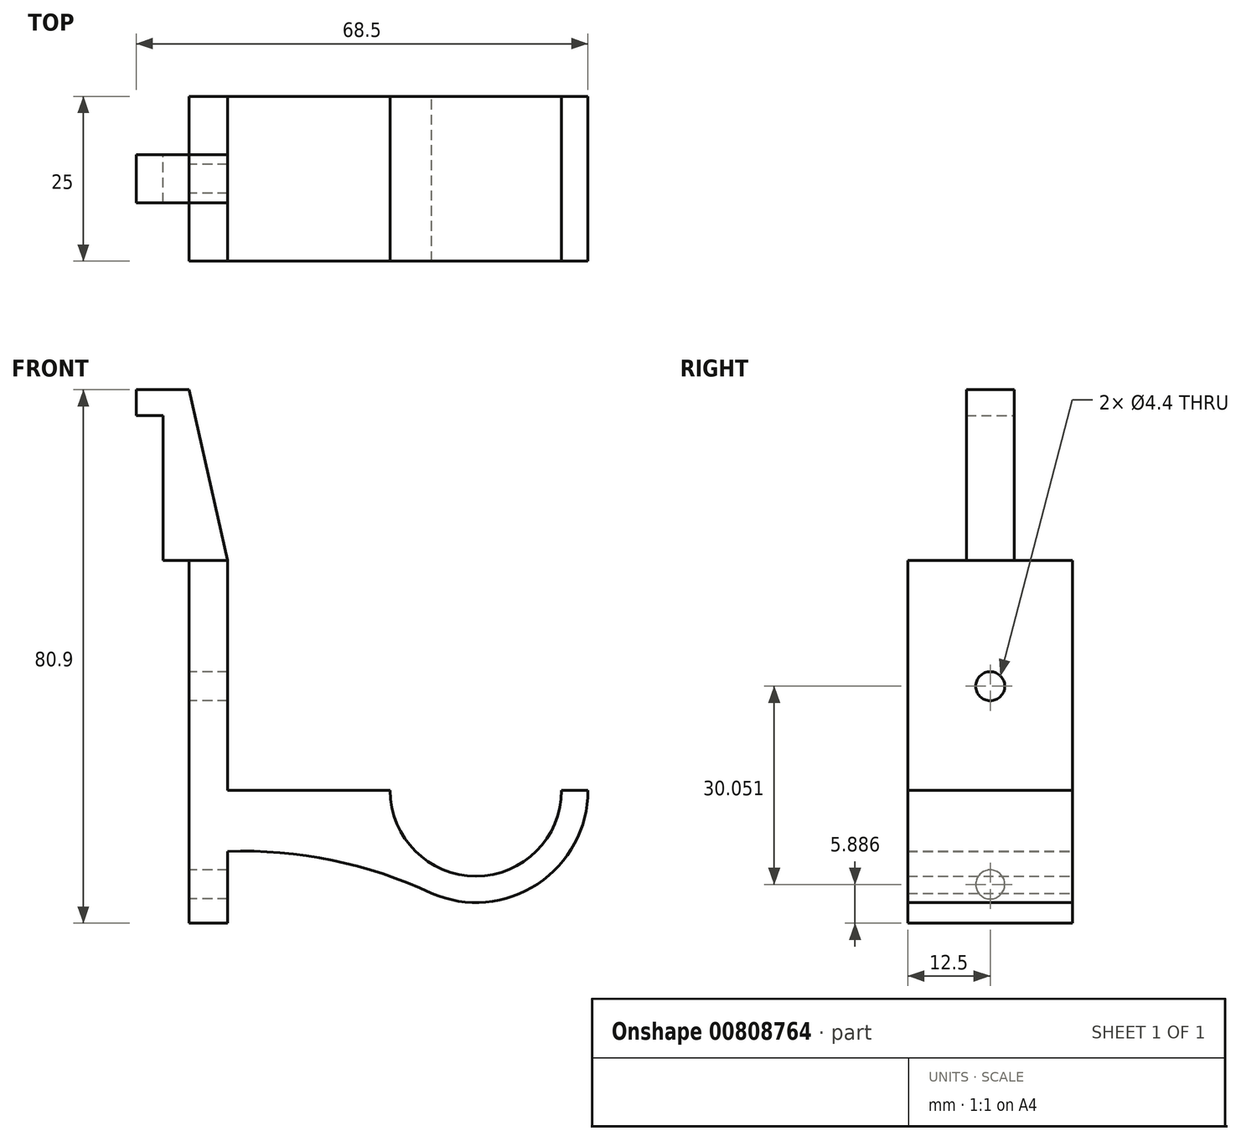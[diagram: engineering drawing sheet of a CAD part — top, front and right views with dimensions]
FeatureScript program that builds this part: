
annotation { "Feature Type Name" : "Feature", "Feature Type Description" : "" }
export const myFeature = defineFeature(function(context is Context, id is Id, definition is map)
    precondition{}
    {
        {
            var Q0;
            Q0=qCreatedBy(makeId("Front.planeOp"),FACE);
            var sketch = newSketch(context, id + "F0", { "sketchPlane" : qUnion([Q0])});
            skLineSegment(sketch, "E0.bottom", {"start": v(-6.93, 34.86) * mm, "end": v(-1.13, 34.86) * mm});
            skLineSegment(sketch, "E0.top", {"start": v(-6.93, -20.14) * mm, "end": v(-1.13, -20.14) * mm});
            skLineSegment(sketch, "E0.left", {"start": v(-6.93, 34.86) * mm, "end": v(-6.93, -20.14) * mm});
            skLineSegment(sketch, "E0.right", {"start": v(-1.13, 34.86) * mm, "end": v(-1.13, -20.14) * mm});
            skLineSegment(sketch, "E1", {"start": v(-6.93, 15.76) * mm, "end": v(-1.13, 15.76) * mm});
            skLineSegment(sketch, "E2", {"start": v(-6.93, -14.24) * mm, "end": v(-1.13, -14.24) * mm});
            skLineSegment(sketch, "E3", {"start": v(-6.93, 34.86) * mm, "end": v(-10.93, 34.86) * mm});
            skLineSegment(sketch, "E4", {"start": v(-10.93, 34.86) * mm, "end": v(-10.93, 56.86) * mm});
            skLineSegment(sketch, "E5", {"start": v(-10.93, 56.86) * mm, "end": v(-15, 56.86) * mm});
            skLineSegment(sketch, "E6", {"start": v(-15, 56.86) * mm, "end": v(-15, 60.76) * mm});
            skLineSegment(sketch, "E7", {"start": v(-15, 60.76) * mm, "end": v(-6.93, 60.76) * mm});
            skLineSegment(sketch, "E8", {"start": v(-6.93, 60.76) * mm, "end": v(-1.13, 34.86) * mm});
            skArc(sketch, "E9", {"start": v(23.53, 0) * mm, "mid": v(36.52, -13) * mm, "end": v(49.51, 0) * mm});
            skArc(sketch, "E10.0", {"start": v(19.53, 0) * mm, "mid": v(36.52, -17) * mm, "end": v(53.51, 0) * mm});
            skArc(sketch, "E11", {"start": v(29.82, -15.62) * mm, "mid": v(14.72, -10.58) * mm, "end": v(-1.13, -9.24) * mm});
            skLineSegment(sketch, "E12", {"start": v(19.53, 0) * mm, "end": v(23.53, 0) * mm});
            skLineSegment(sketch, "E13", {"start": v(53.51, 0) * mm, "end": v(53.51, 0) * mm});
            skLineSegment(sketch, "E14", {"start": v(49.51, 0) * mm, "end": v(53.51, 0) * mm});
            skLineSegment(sketch, "E15", {"start": v(19.53, 0) * mm, "end": v(-1.13, 0) * mm});
            skPoint(sketch, "E15.endSnap0", {"position": v(-1.13, 7.36) * mm});
            skSolve(sketch);
        }
        {
            var Q0;
            {var subQ0=sQuery(id+"F0.wireOp",EDGE,"E0.top");Q0=makeQuery(id+"F0.imprint","IMPRINT",FACE,{"disambiguationData":[TD([[makeQuery(id+"F0.imprint","IMPRINT",EDGE,{"derivedFrom":subQ0}),1.0]])]});}
            var Q1;
            {var subQ0=sQuery(id+"F0.wireOp",EDGE,"E11");var subQ1=sQuery(id+"F0.wireOp",EDGE,"E10.0");var subQ2=makeQuery(id+"F0.imprint","INTERSECT",VERTEX,{"disambiguationData":[OD(0.0)],"derivedFrom":[subQ1,subQ0]});Q1=makeQuery(id+"F0.imprint","IMPRINT",FACE,{"disambiguationData":[TD([[makeQuery(id+"F0.imprint","IMPRINT",EDGE,{"disambiguationData":[TD([[subQ2,1.0]])],"derivedFrom":subQ1}),1.0]])]});}
            var Q2;
            {var subQ0=sQuery(id+"F0.wireOp",EDGE,"E0.bottom");Q2=makeQuery(id+"F0.imprint","IMPRINT",FACE,{"disambiguationData":[TD([[makeQuery(id+"F0.imprint","IMPRINT",EDGE,{"derivedFrom":subQ0}),-1.0]])]});}
            var Q3;
            {var subQ3=sQuery(id+"F0.wireOp",EDGE,"E15");Q3=makeQuery(id+"F0.imprint","IMPRINT",FACE,{"disambiguationData":[TD([[makeQuery(id+"F0.imprint","IMPRINT",EDGE,{"derivedFrom":subQ3}),1.0]])]});}
            var Q4;
            Q4=makeQuery(id+"F0.imprint","IMPRINT",FACE,{"disambiguationData":[TD([[makeQuery(id+"F0.imprint","IMPRINT",EDGE,{"derivedFrom":sQuery(id+"F0.wireOp",EDGE,"E9")}),-1.0]])]});
            var Q5;
            {var subQ3=sQuery(id+"F0.wireOp",EDGE,"E1");Q5=makeQuery(id+"F0.imprint","IMPRINT",FACE,{"disambiguationData":[TD([[makeQuery(id+"F0.imprint","IMPRINT",EDGE,{"derivedFrom":subQ3}),-1.0]])]});}
            extrude(context, id + "F1", {"entities" : qUnion([Q0, Q1, Q2, Q3, Q4, Q5]), "endBound" : BoundingType.SYMMETRIC, "depth" : 25 * mm, "offsetDistance" : 25 * mm});
        }
        {
            var Q0;
            Q0=makeQuery(id+"F1.opExtrude","SWEPT_FACE",FACE,{"disambiguationData":[OSD([sQuery(id+"F0.wireOp",EDGE,"E0.left")])]});
            var sketch = newSketch(context, id + "F2", { "sketchPlane" : qUnion([Q0])});
            skLineSegment(sketch, "E16", {"start": v(0, 15.8) * mm, "end": v(0, -14.25) * mm});
            skSolve(sketch);
        }
        {
            var Q0;
            Q0=sQuery(id+"F2.wireOp",VERTEX,"E16.start");
            var Q1;
            Q1=sQuery(id+"F2.wireOp",VERTEX,"E16.end");
            var Q2;
            Q2=makeQuery(id+"F1.opExtrude","SWEPT_BODY",BODY,{"disambiguationData":[OSD([sQuery(id+"F0.wireOp",EDGE,"E0.bottom"),sQuery(id+"F0.wireOp",EDGE,"E0.top"),sQuery(id+"F0.wireOp",EDGE,"E0.left"),sQuery(id+"F0.wireOp",EDGE,"E0.right"),sQuery(id+"F0.wireOp",EDGE,"E9"),sQuery(id+"F0.wireOp",EDGE,"E10.0"),sQuery(id+"F0.wireOp",EDGE,"E11"),sQuery(id+"F0.wireOp",EDGE,"E12"),sQuery(id+"F0.wireOp",EDGE,"E14"),sQuery(id+"F0.wireOp",EDGE,"E15")])]});
            hole(context, id + "F3", {"style" : HoleStyle.SIMPLE, "endStyle" : HoleEndStyle.BLIND, "standardTappedOrClearance" : lookupTablePath({ "standard" : "ISO", "fit" : "Normal", "size" : "M4", "type" : "Clearance" }), "standardBlindInLast" : lookupTablePath({ "fit" : "Standard", "standard" : "ISO", "size" : "M4", "type" : "Clearance" }), "holeDiameter" : 4.4 * mm, "majorDiameter" : 4 * mm, "holeDepth" : 14.1 * mm, "isTappedThrough" : true, "tappedDepth" : 12 * mm, "tapClearance" : 3, "locations" : qUnion([Q0, Q1]), "scope" : qUnion([Q2])});
        }
        {
            var Q0;
            Q0=makeQuery(id+"F0.imprint","IMPRINT",FACE,{"disambiguationData":[TD([[makeQuery(id+"F0.imprint","IMPRINT",EDGE,{"derivedFrom":sQuery(id+"F0.wireOp",EDGE,"E0.bottom")}),1.0]])]});
            extrude(context, id + "F4", {"entities" : qUnion([Q0]), "operationType" : NewBodyOperationType.ADD, "endBound" : BoundingType.SYMMETRIC, "depth" : 7.25 * mm, "offsetDistance" : 25 * mm});
        }
    });
